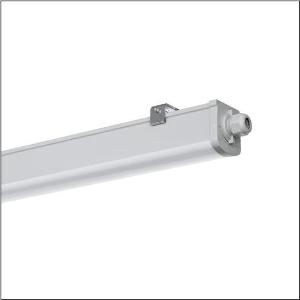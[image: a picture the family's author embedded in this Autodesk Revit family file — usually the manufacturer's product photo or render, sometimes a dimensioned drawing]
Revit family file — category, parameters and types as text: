
# Revit family: monsun_r__31_51fa20dk430b_aae0
name_source: partatom
category: Lighting Fixtures
units: mm (PartAtom-declared; Revit-internal decimal feet)

## family parameters
Cut with Voids When Loaded = No
Host = Face
Light Source = No
Part Type = Normal
Room Calculation Point = No
Round Connector Dimension = Use Diameter
Shared = No

## types (1)
- Monsun® 31 (1 x LED, 3000 lm, 22 W, 4000K)
    Apparent Load = 22 VA
    CIE Flux Codes = 42 72 91 92 100
    Color Rendering = 80
    Color Temperature = 4000K
    Default Elevation = 1800 mm
    Description = Monsun® 31, damp-proof luminaire, primary optical cover: diffuser, of PC, frosted, light emission: direct distribution, primary light characteristic: symmetric, installation type: surface-mounted, LED, rated luminous flux: 3.000lm, luminous efficacy: 136lm/W, light colour: 840, colour temperature: 4000K, control gear: ECG, with terminal, 5+1-pole, max. 2.5mm², through-wiring: 3x 2.5mm² + 3x 1.5mm², mains connection: 220..240V, AC, 50/60Hz, rated input power: 22W, housing, luminaire housing, of PC, light grey (RAL 7035), length: 1.158mm, width: 68mm, height: 76mm, protection rating (complete): IP66, insulation class (complete): insulation class II (safety insulation), certification: CE, ENEC, UKCA, protection symbol: D, impact resistance: IK08, permissible operating ambient temperature: -20..+40°C, corresponds to IFS (International Featured Standards) requirements for safety and quality in the food industry, contact your sales advisor before using the luminaires in applications with unclear chemical exposure, large temperature fluctuations or condensation-forming humidity, packaging unit: 1 piece
    Height = 77 mm
    Lamp = 1 x LED
    Lamp Light Flux = 3000 lm
    Lamp Power = 22 W
    Lamp count = 1
    Length = 1218 mm
    Luminous efficacy = 136 lm/W
    Manufacturer = Siteco
    ModVariant = No
    Model = 51FA20DK430B
    Mounting Place = Ceiling
    Mounting Type = Surface mounted
    Number of Poles = 1
    OnlyDefault = Yes
    Power Factor = 1
    Product Name = Monsun® 31
    Product group = damp-proof luminaire
    ProductGroupID = 300
    Protection Class = Protection class II
    Protection Degree = IP 66
    RLX_Detail_Level = 1
    RLX_Emergency_Light_Flux = 0 lm
    RLX_Emergency_Type = 0
    RLX_Emergency_Type_DB = No
    RlxData = <blob elided: 32809 chars, md5=083949d9>
    Socket = socket
    Standby Power = 0 W
    System Light Flux = 3000 lm
    System Power = 22 W
    Type Comments = Product without accessories
    Type Image = l_1006174.jpg
    URL = http://relux.com
    VarID = ---
    Voltage = 0 V
    Weight = 0.00 kg
    Width = 69 mm

## geometry (parser evidence)
native form markers: Blend x4, Sweep x13
no freeform markers — native parametric forms only
